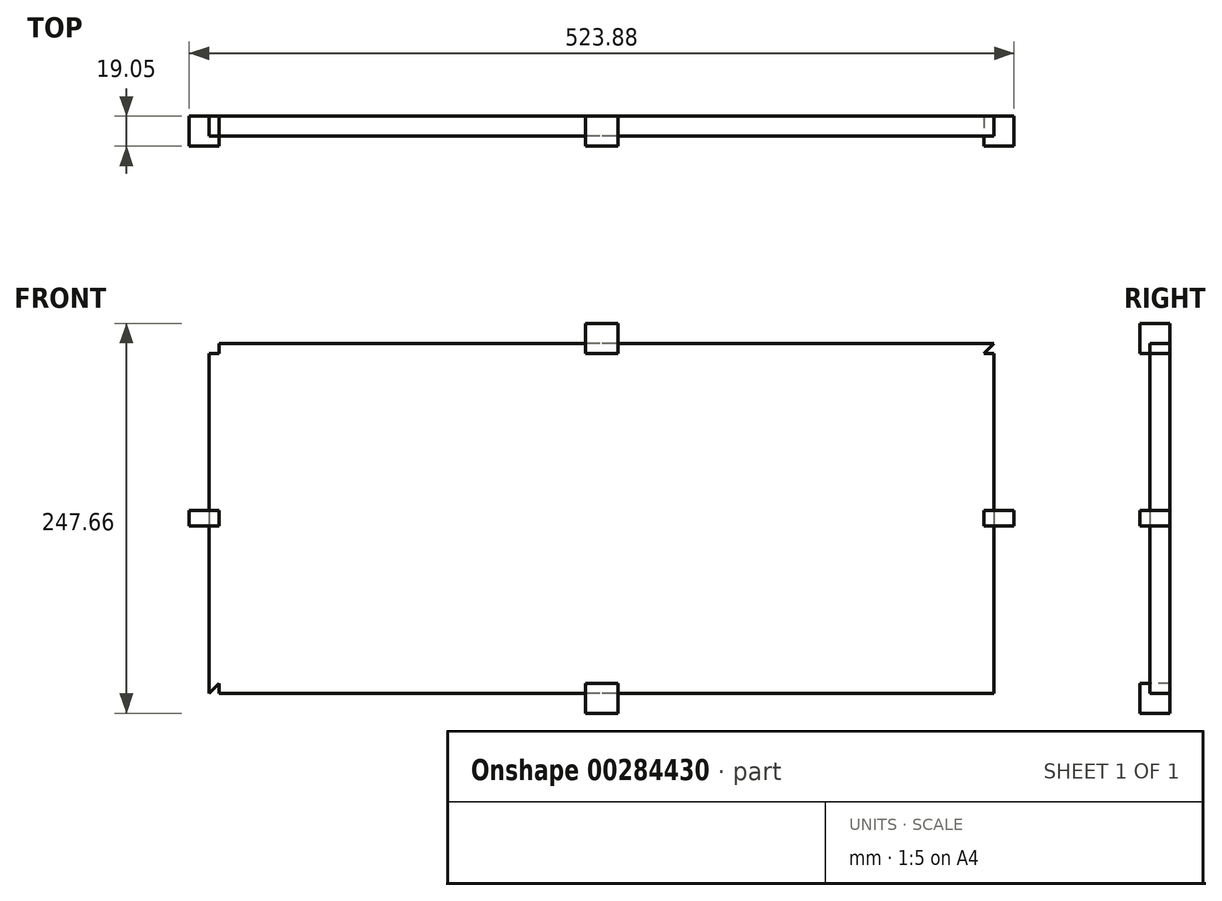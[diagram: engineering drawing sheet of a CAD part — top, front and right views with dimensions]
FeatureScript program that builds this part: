
annotation { "Feature Type Name" : "Feature", "Feature Type Description" : "" }
export const myFeature = defineFeature(function(context is Context, id is Id, definition is map)
    precondition{}
    {
        {
            assignVariable(context, id + "F0", {"name" : "Width", "anyValue" : 20.62});
        }
        {
            assignVariable(context, id + "F1", {"name" : "Height", "anyValue" : 9.75});
        }
        {
            var Q0;
            Q0=qCreatedBy(makeId("Front.planeOp"),FACE);
            var sketch = newSketch(context, id + "F2", { "sketchPlane" : qUnion([Q0])});
            skLineSegment(sketch, "E0.bottom", {"start": v(249.24, 111.13) * mm, "end": v(-249.24, 111.13) * mm});
            skLineSegment(sketch, "E0.top", {"start": v(249.24, -111.12) * mm, "end": v(-249.24, -111.12) * mm});
            skLineSegment(sketch, "E0.left", {"start": v(249.24, 111.13) * mm, "end": v(249.24, -111.12) * mm});
            skLineSegment(sketch, "E0.right", {"start": v(-249.24, 111.13) * mm, "end": v(-249.24, -111.12) * mm});
            skPoint(sketch, "E0.middle", {"position": v(0, 0) * mm});
            skSolve(sketch);
        }
        {
            var Q0;
            Q0=makeQuery(id+"F2.imprint","IMPRINT",FACE,{"disambiguationData":[TD([[makeQuery(id+"F2.imprint","IMPRINT",EDGE,{"derivedFrom":sQuery(id+"F2.wireOp",EDGE,"E0.bottom")}),1.0]])]});
            extrude(context, id + "F3", {"entities" : qUnion([Q0]), "depth" : 12.7 * mm});
        }
        {
            var Q0;
            Q0=qCreatedBy(makeId("Top.planeOp"),FACE);
            var sketch = newSketch(context, id + "F4", { "sketchPlane" : qUnion([Q0])});
            skLineSegment(sketch, "E1", {"start": v(-261.94, 0) * mm, "end": v(-261.94, -19.05) * mm});
            skLineSegment(sketch, "E2", {"start": v(-261.94, -19.05) * mm, "end": v(-242.89, -19.05) * mm});
            skLineSegment(sketch, "E3", {"start": v(-242.89, -19.05) * mm, "end": v(-242.89, -12.7) * mm});
            skLineSegment(sketch, "E4", {"start": v(-242.89, -12.7) * mm, "end": v(-249.24, -12.7) * mm});
            skLineSegment(sketch, "E5", {"start": v(-249.24, -12.7) * mm, "end": v(-249.24, 0) * mm});
            skLineSegment(sketch, "E6", {"start": v(-249.24, 0) * mm, "end": v(-261.94, 0) * mm});
            skSolve(sketch);
        }
        {
            var Q0;
            Q0=makeQuery(id+"F4.imprint","IMPRINT",FACE,{"disambiguationData":[TD([[makeQuery(id+"F4.imprint","IMPRINT",EDGE,{"derivedFrom":sQuery(id+"F4.wireOp",EDGE,"E1")}),1.0]])]});
            extrude(context, id + "F5", {"entities" : qUnion([Q0]), "depth" : (getVariable(context, 'Height') / 2) * mm, "hasSecondDirection" : true, "secondDirectionOppositeDirection" : true, "secondDirectionDepth" : (getVariable(context, 'Height') / 2) * mm});
        }
        {
            var Q0;
            Q0=makeQuery(id+"F5.opExtrude","SWEPT_FACE",FACE,{"disambiguationData":[OSD([sQuery(id+"F4.wireOp",EDGE,"E2")])]});
            var sketch = newSketch(context, id + "F6", { "sketchPlane" : qUnion([Q0])});
            skLineSegment(sketch, "E7", {"start": v(-261.94, 123.83) * mm, "end": v(-242.89, 104.78) * mm});
            skLineSegment(sketch, "E8", {"start": v(-242.89, 104.78) * mm, "end": v(-242.89, 123.83) * mm});
            skLineSegment(sketch, "E9", {"start": v(-242.89, 123.83) * mm, "end": v(-261.94, 123.83) * mm});
            skLineSegment(sketch, "E10.MirrorCS", {"start": v(-261.94, -123.83) * mm, "end": v(-242.89, -104.78) * mm});
            skLineSegment(sketch, "E11.MirrorCS", {"start": v(-242.89, -104.78) * mm, "end": v(-242.89, -123.83) * mm});
            skLineSegment(sketch, "E12.MirrorCS", {"start": v(-242.89, -123.83) * mm, "end": v(-261.94, -123.83) * mm});
            skSolve(sketch);
        }
        {
            var Q0;
            Q0=qSketchRegion(id+"F6",true);
            extrude(context, id + "F7", {"entities" : qUnion([Q0]), "operationType" : NewBodyOperationType.REMOVE, "endBound" : BoundingType.THROUGH_ALL, "oppositeDirection" : true, "depth" : 25.4 * mm});
        }
        {
            var Q0;
            Q0=qCreatedBy(makeId("Right.planeOp"),FACE);
            var sketch = newSketch(context, id + "F8", { "sketchPlane" : qUnion([Q0])});
            skLineSegment(sketch, "E13", {"start": v(0, 123.83) * mm, "end": v(-19.05, 123.83) * mm});
            skLineSegment(sketch, "E14", {"start": v(-19.05, 123.83) * mm, "end": v(-19.05, 104.78) * mm});
            skLineSegment(sketch, "E15", {"start": v(-19.05, 104.78) * mm, "end": v(-12.7, 104.78) * mm});
            skLineSegment(sketch, "E16", {"start": v(-12.7, 104.78) * mm, "end": v(-12.7, 111.13) * mm});
            skLineSegment(sketch, "E17", {"start": v(-12.7, 111.13) * mm, "end": v(0, 111.13) * mm});
            skLineSegment(sketch, "E18", {"start": v(0, 111.13) * mm, "end": v(0, 123.83) * mm});
            skSolve(sketch);
        }
        {
            var Q0;
            Q0=qSketchRegion(id+"F8",true);
            extrude(context, id + "F9", {"entities" : qUnion([Q0]), "depth" : (getVariable(context, 'Width') / 2) * mm, "hasSecondDirection" : true, "secondDirectionOppositeDirection" : true, "secondDirectionDepth" : (getVariable(context, 'Width') / 2) * mm});
        }
        {
            var Q0;
            Q0=makeQuery(id+"F9.opExtrude","SWEPT_FACE",FACE,{"disambiguationData":[OSD([sQuery(id+"F8.wireOp",EDGE,"E14")])]});
            var sketch = newSketch(context, id + "F10", { "sketchPlane" : qUnion([Q0])});
            skLineSegment(sketch, "E19", {"start": v(-261.94, 123.83) * mm, "end": v(-242.89, 104.78) * mm});
            skLineSegment(sketch, "E20", {"start": v(-242.89, 104.78) * mm, "end": v(-261.94, 104.78) * mm});
            skLineSegment(sketch, "E21", {"start": v(-261.94, 104.78) * mm, "end": v(-261.94, 123.83) * mm});
            skLineSegment(sketch, "E22.MirrorCS", {"start": v(242.89, 104.78) * mm, "end": v(261.94, 104.78) * mm});
            skLineSegment(sketch, "E23.MirrorCS", {"start": v(261.94, 104.78) * mm, "end": v(261.94, 123.83) * mm});
            skLineSegment(sketch, "E24.MirrorCS", {"start": v(261.94, 123.83) * mm, "end": v(242.89, 104.78) * mm});
            skSolve(sketch);
        }
        {
            var Q0;
            Q0=qSketchRegion(id+"F10",true);
            extrude(context, id + "F11", {"entities" : qUnion([Q0]), "operationType" : NewBodyOperationType.REMOVE, "endBound" : BoundingType.THROUGH_ALL, "oppositeDirection" : true, "depth" : 25.4 * mm});
        }
        {
            var Q0;
            Q0=makeQuery(id+"F5.opExtrude","SWEPT_BODY",BODY,{"disambiguationData":[OSD([sQuery(id+"F4.wireOp",EDGE,"E1"),sQuery(id+"F4.wireOp",EDGE,"E2"),sQuery(id+"F4.wireOp",EDGE,"E3"),sQuery(id+"F4.wireOp",EDGE,"E4"),sQuery(id+"F4.wireOp",EDGE,"E5"),sQuery(id+"F4.wireOp",EDGE,"E6")])]});
            var Q1;
            Q1=qCreatedBy(makeId("Right.planeOp"),FACE);
            mirror(context, id + "F12", {"entities" : qUnion([Q0]), "mirrorPlane" : qUnion([Q1])});
        }
        {
            var Q0;
            Q0=makeQuery(id+"F9.opExtrude","SWEPT_BODY",BODY,{"disambiguationData":[OSD([sQuery(id+"F8.wireOp",EDGE,"E13"),sQuery(id+"F8.wireOp",EDGE,"E14"),sQuery(id+"F8.wireOp",EDGE,"E15"),sQuery(id+"F8.wireOp",EDGE,"E16"),sQuery(id+"F8.wireOp",EDGE,"E17"),sQuery(id+"F8.wireOp",EDGE,"E18")])]});
            var Q1;
            Q1=qCreatedBy(makeId("Top.planeOp"),FACE);
            mirror(context, id + "F13", {"entities" : qUnion([Q0]), "mirrorPlane" : qUnion([Q1])});
        }
    });
